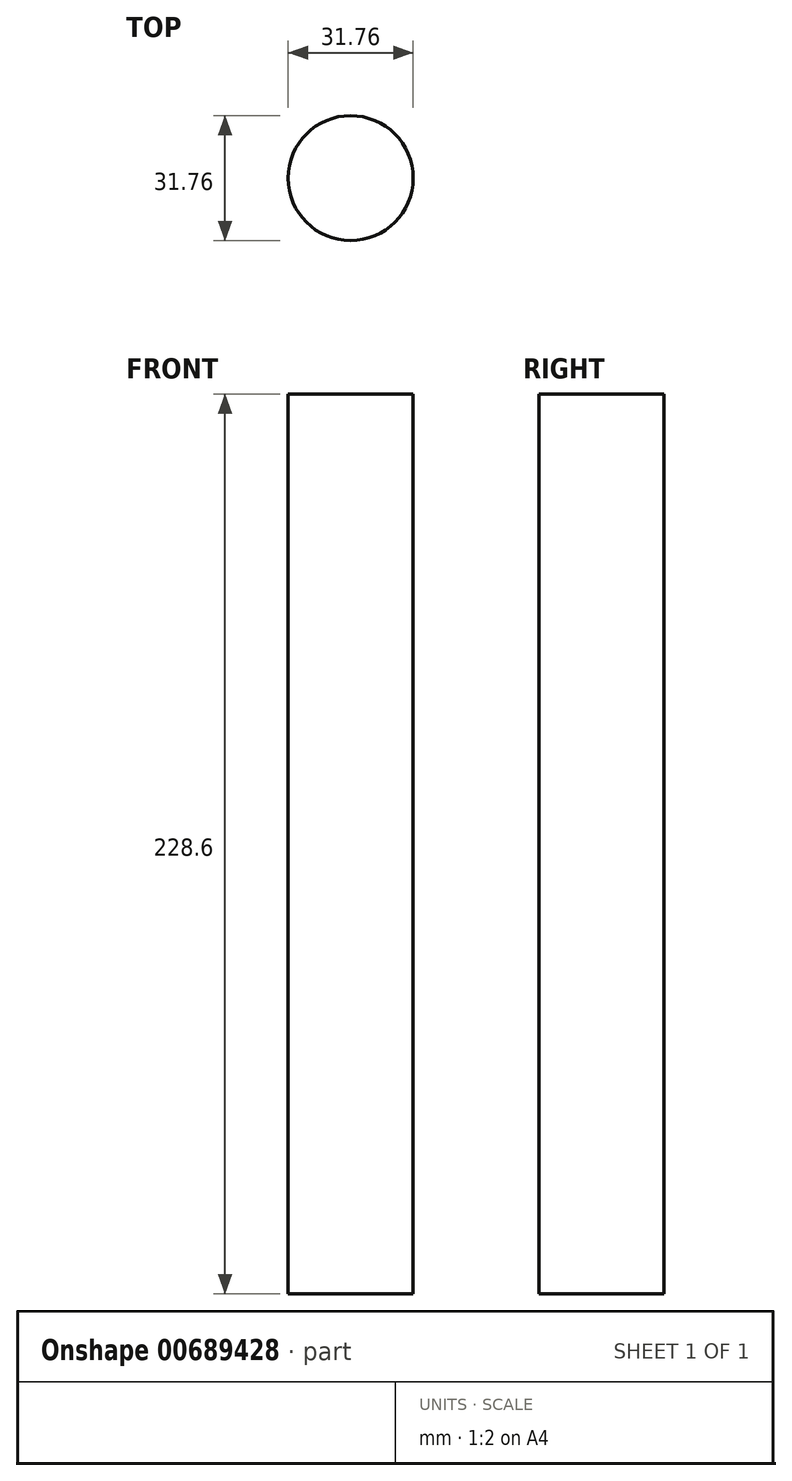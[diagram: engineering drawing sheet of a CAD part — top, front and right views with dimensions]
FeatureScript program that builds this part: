
annotation { "Feature Type Name" : "Feature", "Feature Type Description" : "" }
export const myFeature = defineFeature(function(context is Context, id is Id, definition is map)
    precondition{}
    {
        {
            var Q0;
            Q0=qCreatedBy(makeId("Top.planeOp"),FACE);
            var sketch = newSketch(context, id + "F0", { "sketchPlane" : qUnion([Q0])});
            skCircle(sketch, "E0", {"center": v(0, 0) * mm, "radius": 15.88 * mm});
            skSolve(sketch);
        }
        {
            var Q0;
            Q0=makeQuery(id+"F0.imprint","IMPRINT",FACE,{"disambiguationData":[TD([[makeQuery(id+"F0.imprint","IMPRINT",EDGE,{"derivedFrom":sQuery(id+"F0.wireOp",EDGE,"E0")}),1.0]])]});
            extrude(context, id + "F1", {"entities" : qUnion([Q0]), "depth" : 228.6 * mm, "offsetDistance" : 25.4 * mm});
        }
    });
